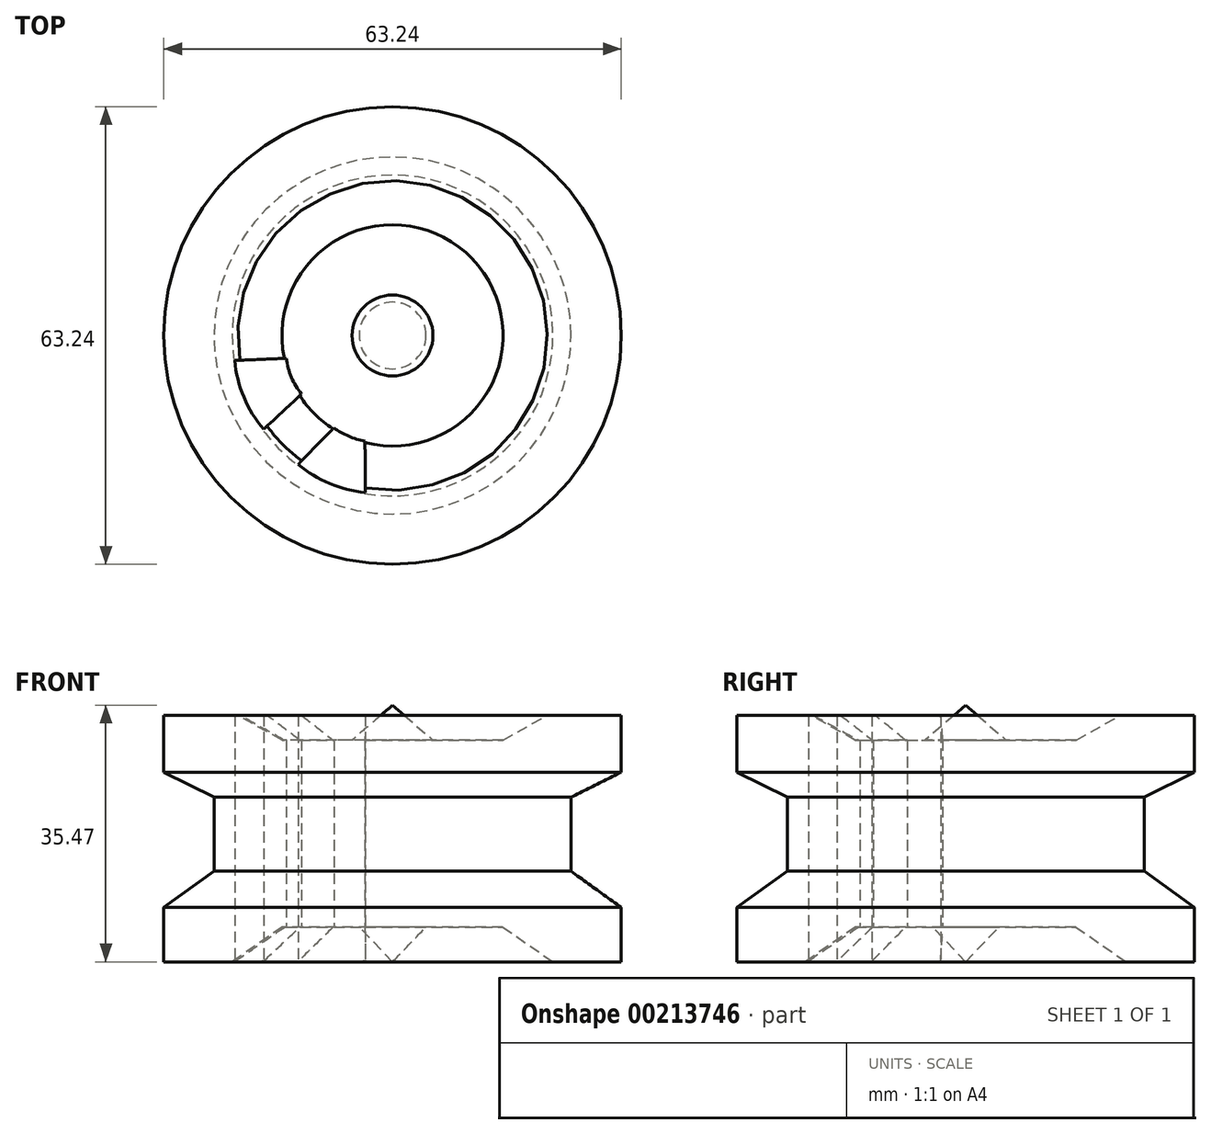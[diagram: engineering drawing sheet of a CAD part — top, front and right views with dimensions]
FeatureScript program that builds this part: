
annotation { "Feature Type Name" : "Feature", "Feature Type Description" : "" }
export const myFeature = defineFeature(function(context is Context, id is Id, definition is map)
    precondition{}
    {
        {
            var Q0;
            Q0=qCreatedBy(makeId("Front.planeOp"),FACE);
            var sketch = newSketch(context, id + "F0", { "sketchPlane" : qUnion([Q0])});
            skLineSegment(sketch, "E0", {"start": v(0, 0) * mm, "end": v(4.62, 4.82) * mm});
            skLineSegment(sketch, "E1", {"start": v(4.62, 4.82) * mm, "end": v(15.23, 4.82) * mm});
            skLineSegment(sketch, "E2", {"start": v(15.23, 4.82) * mm, "end": v(22.17, 0) * mm});
            skLineSegment(sketch, "E3", {"start": v(22.17, 0) * mm, "end": v(24.87, 0) * mm});
            skLineSegment(sketch, "E4", {"start": v(24.87, 0) * mm, "end": v(31.62, 0) * mm});
            skLineSegment(sketch, "E5", {"start": v(31.62, 0) * mm, "end": v(31.62, 7.52) * mm});
            skLineSegment(sketch, "E6", {"start": v(31.62, 7.52) * mm, "end": v(24.68, 12.53) * mm});
            skLineSegment(sketch, "E7", {"start": v(24.68, 12.53) * mm, "end": v(24.68, 22.75) * mm});
            skLineSegment(sketch, "E8", {"start": v(24.68, 22.75) * mm, "end": v(31.62, 26.22) * mm});
            skLineSegment(sketch, "E9", {"start": v(31.62, 26.22) * mm, "end": v(31.62, 34.08) * mm});
            skLineSegment(sketch, "E10", {"start": v(31.62, 34.08) * mm, "end": v(21.4, 34.08) * mm});
            skLineSegment(sketch, "E11", {"start": v(21.4, 34.08) * mm, "end": v(15.3, 30.65) * mm});
            skLineSegment(sketch, "E12", {"start": v(15.3, 30.65) * mm, "end": v(5.6, 30.65) * mm});
            skLineSegment(sketch, "E13", {"start": v(5.6, 30.65) * mm, "end": v(0, 35.47) * mm});
            skLineSegment(sketch, "E14", {"start": v(0, 35.47) * mm, "end": v(0, 0) * mm});
            skSolve(sketch);
        }
        {
            var Q0;
            Q0=makeQuery(id+"F0.imprint","IMPRINT",FACE,{"disambiguationData":[TD([[makeQuery(id+"F0.imprint","IMPRINT",EDGE,{"derivedFrom":sQuery(id+"F0.wireOp",EDGE,"E0")}),1.0]])]});
            var Q1;
            Q1=sQuery(id+"F0.wireOp",EDGE,"E14");
            revolve(context, id + "F1", {"entities" : qUnion([Q0]), "axis" : qUnion([Q1]), "revolveType" : RevolveType.FULL});
        }
        {
            var Q0;
            Q0=qCreatedBy(makeId("Top.planeOp"),FACE);
            var sketch = newSketch(context, id + "F2", { "sketchPlane" : qUnion([Q0])});
            skArc(sketch, "E15", {"start": v(-13.05, -17.82) * mm, "mid": v(-8.7, -20.46) * mm, "end": v(-3.78, -21.72) * mm});
            skArc(sketch, "E16", {"start": v(-21.81, -3.46) * mm, "mid": v(-20.56, -8.53) * mm, "end": v(-17.82, -12.97) * mm});
            skArc(sketch, "E17", {"start": v(-8.12, -12.75) * mm, "mid": v(-6.07, -13.93) * mm, "end": v(-3.8, -14.61) * mm});
            skArc(sketch, "E18", {"start": v(-14.67, -3.16) * mm, "mid": v(-13.98, -5.78) * mm, "end": v(-12.59, -8.1) * mm});
            skLineSegment(sketch, "E19", {"start": v(-14.67, -3.16) * mm, "end": v(-21.81, -3.46) * mm});
            skLineSegment(sketch, "E20", {"start": v(-12.59, -8.1) * mm, "end": v(-17.82, -12.97) * mm});
            skLineSegment(sketch, "E21", {"start": v(-13.05, -17.82) * mm, "end": v(-8.12, -12.75) * mm});
            skLineSegment(sketch, "E22", {"start": v(-3.78, -21.72) * mm, "end": v(-3.8, -14.61) * mm});
            skSolve(sketch);
        }
        {
            var Q0;
            Q0=makeQuery(id+"F2.imprint","IMPRINT",FACE,{"disambiguationData":[TD([[makeQuery(id+"F2.imprint","IMPRINT",EDGE,{"derivedFrom":sQuery(id+"F2.wireOp",EDGE,"E15")}),1.0]])]});
            var Q1;
            Q1=makeQuery(id+"F2.imprint","IMPRINT",FACE,{"disambiguationData":[TD([[makeQuery(id+"F2.imprint","IMPRINT",EDGE,{"derivedFrom":sQuery(id+"F2.wireOp",EDGE,"E16")}),1.0]])]});
            var Q2;
            Q2=makeQuery(id+"Fen1dJYTvJ3S6rX_1.1.F2.imprint","IMPRINT",FACE,{"disambiguationData":[TD([[makeQuery(id+"Fen1dJYTvJ3S6rX_1.1.F2.imprint","IMPRINT",EDGE,{"derivedFrom":sQuery(id+"Fen1dJYTvJ3S6rX_1.1.F2.wireOp",EDGE,"E16")}),1.0]])]});
            var Q3;
            Q3=makeQuery(id+"Fen1dJYTvJ3S6rX_1.1.F2.imprint","IMPRINT",FACE,{"disambiguationData":[TD([[makeQuery(id+"Fen1dJYTvJ3S6rX_1.1.F2.imprint","IMPRINT",EDGE,{"derivedFrom":sQuery(id+"Fen1dJYTvJ3S6rX_1.1.F2.wireOp",EDGE,"E15")}),1.0]])]});
            var Q4;
            Q4=makeQuery(id+"Fen1dJYTvJ3S6rX_1.2.F2.imprint","IMPRINT",FACE,{"disambiguationData":[TD([[makeQuery(id+"Fen1dJYTvJ3S6rX_1.2.F2.imprint","IMPRINT",EDGE,{"derivedFrom":sQuery(id+"Fen1dJYTvJ3S6rX_1.2.F2.wireOp",EDGE,"E16")}),1.0]])]});
            var Q5;
            Q5=makeQuery(id+"Fen1dJYTvJ3S6rX_1.2.F2.imprint","IMPRINT",FACE,{"disambiguationData":[TD([[makeQuery(id+"Fen1dJYTvJ3S6rX_1.2.F2.imprint","IMPRINT",EDGE,{"derivedFrom":sQuery(id+"Fen1dJYTvJ3S6rX_1.2.F2.wireOp",EDGE,"E15")}),1.0]])]});
            var Q6;
            Q6=makeQuery(id+"Fen1dJYTvJ3S6rX_1.3.F2.imprint","IMPRINT",FACE,{"disambiguationData":[TD([[makeQuery(id+"Fen1dJYTvJ3S6rX_1.3.F2.imprint","IMPRINT",EDGE,{"derivedFrom":sQuery(id+"Fen1dJYTvJ3S6rX_1.3.F2.wireOp",EDGE,"E16")}),1.0]])]});
            var Q7;
            Q7=makeQuery(id+"Fen1dJYTvJ3S6rX_1.3.F2.imprint","IMPRINT",FACE,{"disambiguationData":[TD([[makeQuery(id+"Fen1dJYTvJ3S6rX_1.3.F2.imprint","IMPRINT",EDGE,{"derivedFrom":sQuery(id+"Fen1dJYTvJ3S6rX_1.3.F2.wireOp",EDGE,"E15")}),1.0]])]});
            extrude(context, id + "F3", {"entities" : qUnion([Q0, Q1, Q2, Q3, Q4, Q5, Q6, Q7]), "operationType" : NewBodyOperationType.REMOVE, "depth" : 127 * mm});
        }
    });
